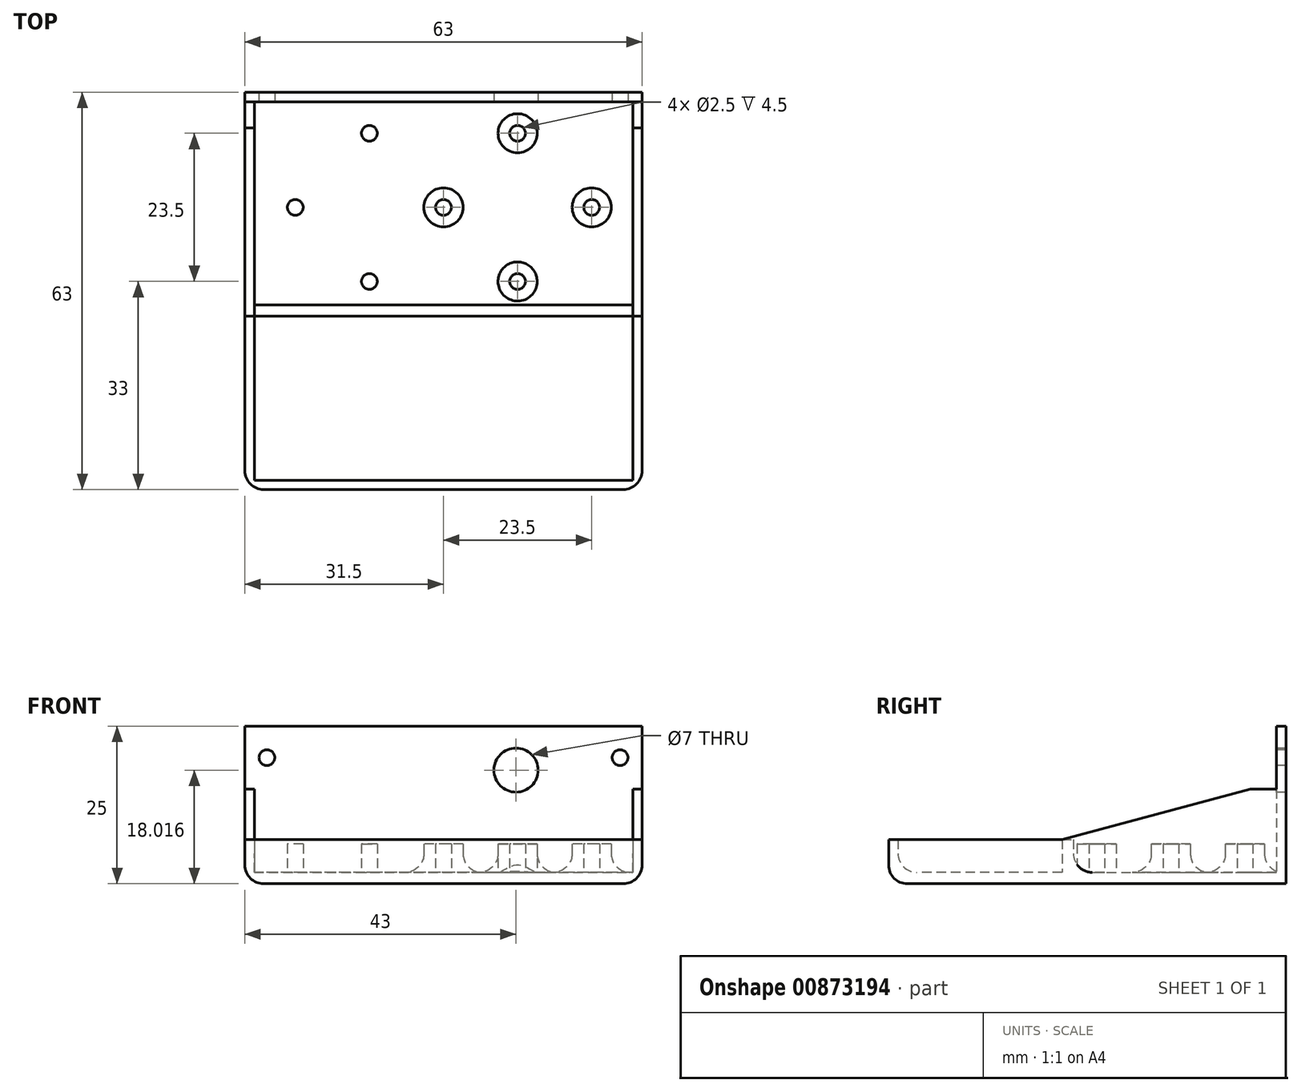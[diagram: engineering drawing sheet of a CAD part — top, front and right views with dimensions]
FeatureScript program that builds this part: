
annotation { "Feature Type Name" : "Feature", "Feature Type Description" : "" }
export const myFeature = defineFeature(function(context is Context, id is Id, definition is map)
    precondition{}
    {
        {
            var Q0;
            Q0=qCreatedBy(makeId("Top.planeOp"),FACE);
            var sketch = newSketch(context, id + "F0", { "sketchPlane" : qUnion([Q0])});
            skLineSegment(sketch, "E0.bottom", {"start": v(30, -30) * mm, "end": v(-30, -30) * mm});
            skLineSegment(sketch, "E0.top", {"start": v(30, 30) * mm, "end": v(-30, 30) * mm});
            skLineSegment(sketch, "E0.left", {"start": v(30, -30) * mm, "end": v(30, 30) * mm});
            skLineSegment(sketch, "E0.right", {"start": v(-30, -30) * mm, "end": v(-30, 30) * mm});
            skPoint(sketch, "E0.middle", {"position": v(0, 0) * mm});
            skLineSegment(sketch, "E1.bottom", {"start": v(31.5, -31.5) * mm, "end": v(-31.5, -31.5) * mm});
            skLineSegment(sketch, "E1.top", {"start": v(31.5, 31.5) * mm, "end": v(-31.5, 31.5) * mm});
            skLineSegment(sketch, "E1.left", {"start": v(31.5, -31.5) * mm, "end": v(31.5, 31.5) * mm});
            skLineSegment(sketch, "E1.right", {"start": v(-31.5, -31.5) * mm, "end": v(-31.5, 31.5) * mm});
            skLineSegment(sketch, "E2.bottom", {"start": v(52.1, -40) * mm, "end": v(-52.1, -40) * mm});
            skLineSegment(sketch, "E2.top", {"start": v(52.1, 40) * mm, "end": v(-52.1, 40) * mm});
            skLineSegment(sketch, "E2.left", {"start": v(52.1, -40) * mm, "end": v(52.1, 40) * mm});
            skLineSegment(sketch, "E2.right", {"start": v(-52.1, -40) * mm, "end": v(-52.1, 40) * mm});
            skLineSegment(sketch, "E3", {"start": v(-31.5, 31.5) * mm, "end": v(-31.5, 40) * mm});
            skLineSegment(sketch, "E4", {"start": v(-31.5, -31.5) * mm, "end": v(-31.5, -40) * mm});
            skLineSegment(sketch, "E5", {"start": v(-21.73, -30) * mm, "end": v(-21.73, -4) * mm, "construction": true});
            skLineSegment(sketch, "E6.bottom", {"start": v(-30, -4) * mm, "end": v(30, -4) * mm});
            skLineSegment(sketch, "E6.top", {"start": v(-30, -2.2) * mm, "end": v(30, -2.2) * mm});
            skLineSegment(sketch, "E6.left", {"start": v(-30, -4) * mm, "end": v(-30, -2.2) * mm});
            skLineSegment(sketch, "E6.right", {"start": v(30, -4) * mm, "end": v(30, -2.2) * mm});
            skLineSegment(sketch, "E7.bottom", {"start": v(-35.7, -5) * mm, "end": v(-31.5, -5) * mm});
            skLineSegment(sketch, "E7.top", {"start": v(-35.7, 5) * mm, "end": v(-31.5, 5) * mm});
            skLineSegment(sketch, "E7.left", {"start": v(-35.7, -5) * mm, "end": v(-35.7, 5) * mm});
            skPoint(sketch, "E7.middle", {"position": v(-31.5, 0) * mm});
            skPoint(sketch, "E7.right.start.orphan", {"position": v(-27.3, -5) * mm});
            skPoint(sketch, "E8.trimOffspring.end.orphan", {"position": v(-27.3, 5) * mm});
            skLineSegment(sketch, "E9.bottom", {"start": v(52.1, -40) * mm, "end": v(64.1, -40) * mm});
            skLineSegment(sketch, "E9.top", {"start": v(52.1, -28) * mm, "end": v(64.1, -28) * mm});
            skLineSegment(sketch, "E9.left", {"start": v(52.1, -40) * mm, "end": v(52.1, -28) * mm});
            skLineSegment(sketch, "E9.right", {"start": v(67.1, -37) * mm, "end": v(67.1, -31) * mm});
            skCircle(sketch, "E10", {"center": v(59.6, -34) * mm, "radius": 1.5 * mm});
            skPoint(sketch, "E10.centerSnap0", {"position": v(67.1, -34) * mm});
            skPoint(sketch, "E10.centerSnap1", {"position": v(59.6, -28) * mm});
            skPoint(sketch, "E11.visualSharp", {"position": v(67.1, -28) * mm});
            skArc(sketch, "E11.filletArc", {"start": v(67.1, -31) * mm, "mid": v(66.22, -28.88) * mm, "end": v(64.1, -28) * mm});
            skPoint(sketch, "E12.visualSharp", {"position": v(67.1, -40) * mm});
            skArc(sketch, "E12.filletArc", {"start": v(64.1, -40) * mm, "mid": v(66.22, -39.12) * mm, "end": v(67.1, -37) * mm});
            skLineSegment(sketch, "E13", {"start": v(0, 0) * mm, "end": v(11.58, 0) * mm, "construction": true});
            skLineSegment(sketch, "E14.MirrorCS", {"start": v(67.1, 37) * mm, "end": v(67.1, 31) * mm});
            skPoint(sketch, "E15.MirrorP", {"position": v(59.6, 28) * mm});
            skCircle(sketch, "E16.MirrorC", {"center": v(59.6, 34) * mm, "radius": 1.5 * mm});
            skLineSegment(sketch, "E17.MirrorCS", {"start": v(52.1, 28) * mm, "end": v(64.1, 28) * mm});
            skPoint(sketch, "E18.MirrorP", {"position": v(67.1, 28) * mm});
            skArc(sketch, "E19.MirrorCS", {"start": v(67.1, 31) * mm, "mid": v(66.22, 28.88) * mm, "end": v(64.1, 28) * mm});
            skPoint(sketch, "E20.MirrorP", {"position": v(67.1, 40) * mm});
            skLineSegment(sketch, "E21.MirrorCS", {"start": v(52.1, 40) * mm, "end": v(64.1, 40) * mm});
            skPoint(sketch, "E22.MirrorP", {"position": v(67.1, 34) * mm});
            skArc(sketch, "E23.MirrorCS", {"start": v(64.1, 40) * mm, "mid": v(66.22, 39.12) * mm, "end": v(67.1, 37) * mm});
            skLineSegment(sketch, "E24", {"start": v(0, 31.5) * mm, "end": v(0, 40) * mm});
            skLineSegment(sketch, "E25", {"start": v(-4, -31.5) * mm, "end": v(-4, -38.7) * mm});
            skLineSegment(sketch, "E26", {"start": v(-4, -38.7) * mm, "end": v(-31.5, -38.7) * mm});
            skLineSegment(sketch, "E27", {"start": v(-4, -38.7) * mm, "end": v(-4, -40) * mm});
            skLineSegment(sketch, "E28", {"start": v(-30, 30) * mm, "end": v(-31.5, 30) * mm});
            skLineSegment(sketch, "E29", {"start": v(30, 30) * mm, "end": v(31.5, 30) * mm});
            skLineSegment(sketch, "E30", {"start": v(-30, -4) * mm, "end": v(-31.5, -4) * mm});
            skLineSegment(sketch, "E31", {"start": v(30, -4) * mm, "end": v(31.5, -4) * mm});
            skSolve(sketch);
        }
        {
            var Q0;
            Q0=makeQuery(id+"F0.imprint","IMPRINT",FACE,{"disambiguationData":[TD([[makeQuery(id+"F0.imprint","IMPRINT",EDGE,{"derivedFrom":sQuery(id+"F0.wireOp",EDGE,"E0.top")}),-1.0]])]});
            extrude(context, id + "F1", {"entities" : qUnion([Q0]), "depth" : 25 * mm, "offsetDistance" : 25 * mm});
        }
        {
            var Q0;
            {var subQ0=sQuery(id+"F0.wireOp",EDGE,"E0.bottom");Q0=makeQuery(id+"F0.imprint","IMPRINT",FACE,{"disambiguationData":[TD([[makeQuery(id+"F0.imprint","IMPRINT",EDGE,{"derivedFrom":subQ0}),-1.0]])]});}
            var Q1;
            {var subQ1=sQuery(id+"F0.wireOp",EDGE,"E0.bottom");Q1=makeQuery(id+"F0.imprint","IMPRINT",FACE,{"disambiguationData":[TD([[makeQuery(id+"F0.imprint","IMPRINT",EDGE,{"derivedFrom":subQ1}),1.0]])]});}
            var Q2;
            {var subQ0=sQuery(id+"F0.wireOp",EDGE,"E0.top");Q2=makeQuery(id+"F0.imprint","IMPRINT",FACE,{"disambiguationData":[TD([[makeQuery(id+"F0.imprint","IMPRINT",EDGE,{"derivedFrom":subQ0}),1.0]])]});}
            var Q3;
            {var subQ2=sQuery(id+"F0.wireOp",EDGE,"E6.bottom");Q3=makeQuery(id+"F0.imprint","IMPRINT",FACE,{"disambiguationData":[TD([[makeQuery(id+"F0.imprint","IMPRINT",EDGE,{"derivedFrom":subQ2}),1.0]])]});}
            extrude(context, id + "F2", {"entities" : qUnion([Q0, Q1, Q2, Q3]), "operationType" : NewBodyOperationType.ADD, "depth" : 1.8 * mm, "offsetDistance" : 25 * mm});
        }
        {
            var Q0;
            {var subQ2=sQuery(id+"F0.wireOp",EDGE,"E6.bottom");Q0=makeQuery(id+"F0.imprint","IMPRINT",FACE,{"disambiguationData":[TD([[makeQuery(id+"F0.imprint","IMPRINT",EDGE,{"derivedFrom":subQ2}),1.0]])]});}
            extrude(context, id + "F3", {"entities" : qUnion([Q0]), "operationType" : NewBodyOperationType.ADD, "depth" : 7 * mm, "offsetDistance" : 25 * mm});
        }
        {
            var Q0;
            Q0=qCreatedBy(makeId("Top.planeOp"),FACE);
            var sketch = newSketch(context, id + "F4", { "sketchPlane" : qUnion([Q0])});
            skLineSegment(sketch, "E32", {"start": v(0, 0) * mm, "end": v(0, 0) * mm});
            skLineSegment(sketch, "E33", {"start": v(0, 0) * mm, "end": v(0, 1.5) * mm, "construction": true});
            skCircle(sketch, "E34", {"center": v(0, 1.5) * mm, "radius": 1.25 * mm});
            skCircle(sketch, "E35", {"center": v(0, 1.5) * mm, "radius": 3.1 * mm});
            skCircle(sketch, "E36.0.1.0", {"center": v(0, 13.25) * mm, "radius": 3.1 * mm});
            skCircle(sketch, "E36.0.1.1", {"center": v(0, 13.25) * mm, "radius": 1.25 * mm});
            skCircle(sketch, "E36.0.2.0", {"center": v(0, 25) * mm, "radius": 3.1 * mm});
            skCircle(sketch, "E36.0.2.1", {"center": v(0, 25) * mm, "radius": 1.25 * mm});
            skCircle(sketch, "E36.1.0.0", {"center": v(11.75, 1.5) * mm, "radius": 3.1 * mm});
            skCircle(sketch, "E36.1.0.1", {"center": v(11.75, 1.5) * mm, "radius": 1.25 * mm});
            skCircle(sketch, "E36.1.1.0", {"center": v(11.75, 13.25) * mm, "radius": 3.1 * mm});
            skCircle(sketch, "E36.1.1.1", {"center": v(11.75, 13.25) * mm, "radius": 1.25 * mm});
            skCircle(sketch, "E36.1.2.0", {"center": v(11.75, 25) * mm, "radius": 3.1 * mm});
            skCircle(sketch, "E36.1.2.1", {"center": v(11.75, 25) * mm, "radius": 1.25 * mm});
            skCircle(sketch, "E36.2.0.0", {"center": v(23.5, 1.5) * mm, "radius": 3.1 * mm});
            skCircle(sketch, "E36.2.0.1", {"center": v(23.5, 1.5) * mm, "radius": 1.25 * mm});
            skCircle(sketch, "E36.2.1.0", {"center": v(23.5, 13.25) * mm, "radius": 3.1 * mm});
            skCircle(sketch, "E36.2.1.1", {"center": v(23.5, 13.25) * mm, "radius": 1.25 * mm});
            skCircle(sketch, "E36.2.2.0", {"center": v(23.5, 25) * mm, "radius": 3.1 * mm});
            skCircle(sketch, "E36.2.2.1", {"center": v(23.5, 25) * mm, "radius": 1.25 * mm});
            skCircle(sketch, "E36.3.0.0", {"center": v(35.25, 1.5) * mm, "radius": 3.1 * mm});
            skCircle(sketch, "E36.3.0.1", {"center": v(35.25, 1.5) * mm, "radius": 1.25 * mm});
            skCircle(sketch, "E36.3.1.0", {"center": v(35.25, 13.25) * mm, "radius": 3.1 * mm});
            skCircle(sketch, "E36.3.1.1", {"center": v(35.25, 13.25) * mm, "radius": 1.25 * mm});
            skCircle(sketch, "E36.3.2.0", {"center": v(35.25, 25) * mm, "radius": 3.1 * mm});
            skCircle(sketch, "E36.3.2.1", {"center": v(35.25, 25) * mm, "radius": 1.25 * mm});
            skCircle(sketch, "E36.4.0.0", {"center": v(47, 1.5) * mm, "radius": 3.1 * mm});
            skCircle(sketch, "E36.4.0.1", {"center": v(47, 1.5) * mm, "radius": 1.25 * mm});
            skCircle(sketch, "E36.4.1.0", {"center": v(47, 13.25) * mm, "radius": 3.1 * mm});
            skCircle(sketch, "E36.4.1.1", {"center": v(47, 13.25) * mm, "radius": 1.25 * mm});
            skCircle(sketch, "E36.4.2.0", {"center": v(47, 25) * mm, "radius": 3.1 * mm});
            skCircle(sketch, "E36.4.2.1", {"center": v(47, 25) * mm, "radius": 1.25 * mm});
            skLineSegment(sketch, "E36.direction1", {"start": v(0, 1.5) * mm, "end": v(11.75, 1.5) * mm, "construction": true});
            skLineSegment(sketch, "E36.direction2", {"start": v(0, 1.5) * mm, "end": v(0, 13.25) * mm, "construction": true});
            skCircle(sketch, "E37.MirrorC", {"center": v(-11.75, 1.5) * mm, "radius": 1.25 * mm});
            skCircle(sketch, "E38.MirrorC", {"center": v(-35.25, 25) * mm, "radius": 1.25 * mm});
            skCircle(sketch, "E39.MirrorC", {"center": v(-47, 25) * mm, "radius": 1.25 * mm});
            skCircle(sketch, "E40.MirrorC", {"center": v(-11.75, 25) * mm, "radius": 1.25 * mm});
            skCircle(sketch, "E41.MirrorC", {"center": v(-47, 1.5) * mm, "radius": 1.25 * mm});
            skCircle(sketch, "E42.MirrorC", {"center": v(-47, 13.25) * mm, "radius": 1.25 * mm});
            skCircle(sketch, "E43.MirrorC", {"center": v(-11.75, 13.25) * mm, "radius": 1.25 * mm});
            skCircle(sketch, "E44.MirrorC", {"center": v(-23.5, 25) * mm, "radius": 1.25 * mm});
            skCircle(sketch, "E45.MirrorC", {"center": v(-23.5, 1.5) * mm, "radius": 1.25 * mm});
            skCircle(sketch, "E46.MirrorC", {"center": v(-35.25, 1.5) * mm, "radius": 1.25 * mm});
            skCircle(sketch, "E47.MirrorC", {"center": v(-35.25, 13.25) * mm, "radius": 1.25 * mm});
            skCircle(sketch, "E48.MirrorC", {"center": v(-23.5, 13.25) * mm, "radius": 1.25 * mm});
            skCircle(sketch, "E49.MirrorC", {"center": v(-11.75, 13.25) * mm, "radius": 3.1 * mm});
            skCircle(sketch, "E50.MirrorC", {"center": v(-35.25, 25) * mm, "radius": 3.1 * mm});
            skCircle(sketch, "E51.MirrorC", {"center": v(-47, 25) * mm, "radius": 3.1 * mm});
            skCircle(sketch, "E52.MirrorC", {"center": v(-35.25, 1.5) * mm, "radius": 3.1 * mm});
            skCircle(sketch, "E53.MirrorC", {"center": v(-47, 13.25) * mm, "radius": 3.1 * mm});
            skCircle(sketch, "E54.MirrorC", {"center": v(-23.5, 25) * mm, "radius": 3.1 * mm});
            skCircle(sketch, "E55.MirrorC", {"center": v(-11.75, 1.5) * mm, "radius": 3.1 * mm});
            skCircle(sketch, "E56.MirrorC", {"center": v(-35.25, 13.25) * mm, "radius": 3.1 * mm});
            skCircle(sketch, "E57.MirrorC", {"center": v(-47, 1.5) * mm, "radius": 3.1 * mm});
            skCircle(sketch, "E58.MirrorC", {"center": v(-11.75, 25) * mm, "radius": 3.1 * mm});
            skCircle(sketch, "E59.MirrorC", {"center": v(-23.5, 1.5) * mm, "radius": 3.1 * mm});
            skCircle(sketch, "E60.MirrorC", {"center": v(-23.5, 13.25) * mm, "radius": 3.1 * mm});
            skCircle(sketch, "E61.MirrorC", {"center": v(-47, -10.25) * mm, "radius": 3.1 * mm});
            skCircle(sketch, "E62.MirrorC", {"center": v(-47, -10.25) * mm, "radius": 1.25 * mm});
            skSolve(sketch);
        }
        {
            var Q0;
            Q0=makeQuery(id+"F4.imprint","IMPRINT",FACE,{"disambiguationData":[TD([[makeQuery(id+"F4.imprint","IMPRINT",EDGE,{"derivedFrom":sQuery(id+"F4.wireOp",EDGE,"E36.2.1.0")}),1.0]])]});
            var Q1;
            Q1=makeQuery(id+"F4.imprint","IMPRINT",FACE,{"disambiguationData":[TD([[makeQuery(id+"F4.imprint","IMPRINT",EDGE,{"derivedFrom":sQuery(id+"F4.wireOp",EDGE,"E36.1.0.0")}),1.0]])]});
            var Q2;
            Q2=makeQuery(id+"F4.imprint","IMPRINT",FACE,{"disambiguationData":[TD([[makeQuery(id+"F4.imprint","IMPRINT",EDGE,{"derivedFrom":sQuery(id+"F4.wireOp",EDGE,"E36.1.2.0")}),1.0]])]});
            var Q3;
            Q3=makeQuery(id+"F4.imprint","IMPRINT",FACE,{"disambiguationData":[TD([[makeQuery(id+"F4.imprint","IMPRINT",EDGE,{"derivedFrom":sQuery(id+"F4.wireOp",EDGE,"E36.0.1.0")}),1.0]])]});
            var Q4;
            Q4=makeQuery(id+"F4.imprint","IMPRINT",FACE,{"disambiguationData":[TD([[makeQuery(id+"F4.imprint","IMPRINT",EDGE,{"derivedFrom":sQuery(id+"F4.wireOp",EDGE,"E40.MirrorC")}),1.0]])]});
            var Q5;
            Q5=makeQuery(id+"F4.imprint","IMPRINT",FACE,{"disambiguationData":[TD([[makeQuery(id+"F4.imprint","IMPRINT",EDGE,{"derivedFrom":sQuery(id+"F4.wireOp",EDGE,"E37.MirrorC")}),1.0]])]});
            var Q6;
            Q6=makeQuery(id+"F4.imprint","IMPRINT",FACE,{"disambiguationData":[TD([[makeQuery(id+"F4.imprint","IMPRINT",EDGE,{"derivedFrom":sQuery(id+"F4.wireOp",EDGE,"E48.MirrorC")}),1.0]])]});
            extrude(context, id + "F5", {"entities" : qUnion([Q0, Q1, Q2, Q3, Q4, Q5, Q6]), "operationType" : NewBodyOperationType.ADD, "depth" : (4.5 + 1.8) * mm, "offsetDistance" : 25 * mm});
        }
        {
            var Q0;
            {var subQ2=sQuery(id+"F0.wireOp",EDGE,"E28");Q0=makeQuery(id+"F0.imprint","IMPRINT",FACE,{"disambiguationData":[TD([[makeQuery(id+"F0.imprint","IMPRINT",EDGE,{"derivedFrom":subQ2}),1.0]])]});}
            var Q1;
            {var subQ0=sQuery(id+"F0.wireOp",EDGE,"E29");Q1=makeQuery(id+"F0.imprint","IMPRINT",FACE,{"disambiguationData":[TD([[makeQuery(id+"F0.imprint","IMPRINT",EDGE,{"derivedFrom":subQ0}),-1.0]])]});}
            extrude(context, id + "F6", {"entities" : qUnion([Q0, Q1]), "operationType" : NewBodyOperationType.ADD, "depth" : 15 * mm, "offsetDistance" : 25 * mm});
        }
        {
            var Q0;
            {var subQ1=sQuery(id+"F0.wireOp",EDGE,"E0.bottom");Q0=makeQuery(id+"F0.imprint","IMPRINT",FACE,{"disambiguationData":[TD([[makeQuery(id+"F0.imprint","IMPRINT",EDGE,{"derivedFrom":subQ1}),1.0]])]});}
            extrude(context, id + "F7", {"entities" : qUnion([Q0]), "operationType" : NewBodyOperationType.ADD, "depth" : 7 * mm, "offsetDistance" : 25 * mm});
        }
        {
            var Q0;
            Q0=makeQuery(id+"F6.opExtrude","CAP_EDGE",EDGE,{"disambiguationData":[OSD([sQuery(id+"F0.wireOp",EDGE,"E30")])],"isStart":false});
            chamfer(context, id + "F8", {"entities" : qUnion([Q0]), "chamferType" : ChamferType.OFFSET_ANGLE, "width" : 8 * mm, "oppositeDirection" : false, "angle" : 75 * degree, "tangentPropagation" : true});
        }
        {
            var Q0;
            Q0=makeQuery(id+"F6.opExtrude","CAP_EDGE",EDGE,{"disambiguationData":[OSD([sQuery(id+"F0.wireOp",EDGE,"E31")])],"isStart":false});
            chamfer(context, id + "F9", {"entities" : qUnion([Q0]), "chamferType" : ChamferType.OFFSET_ANGLE, "width" : 8 * mm, "oppositeDirection" : true, "angle" : 75 * degree, "tangentPropagation" : true});
        }
        {
            var Q0;
            Q0=qCreatedBy(makeId("Front.planeOp"),FACE);
            var sketch = newSketch(context, id + "F10", { "sketchPlane" : qUnion([Q0])});
            skLineSegment(sketch, "E63", {"start": v(0, 0) * mm, "end": v(0, 20) * mm, "construction": true});
            skLineSegment(sketch, "E64", {"start": v(0, 20) * mm, "end": v(28, 20) * mm, "construction": true});
            skCircle(sketch, "E65", {"center": v(28, 20) * mm, "radius": 1.25 * mm});
            skCircle(sketch, "E66.MirrorC", {"center": v(-28, 20) * mm, "radius": 1.25 * mm});
            skLineSegment(sketch, "E67", {"start": v(0, 18.02) * mm, "end": v(11.5, 18.02) * mm, "construction": true});
            skCircle(sketch, "E68", {"center": v(11.5, 18.02) * mm, "radius": 3.5 * mm});
            skSolve(sketch);
        }
        {
            var Q0;
            Q0 = qSketchRegion(id + "F10", true);
            extrude(context, id + "F11", {"entities" : qUnion([Q0]), "operationType" : NewBodyOperationType.REMOVE, "endBound" : BoundingType.THROUGH_ALL, "oppositeDirection" : true, "depth" : 25 * mm, "offsetDistance" : 25 * mm});
        }
        {
            var Q0;
            Q0=makeQuery(id+"F2.opExtrude","CAP_EDGE",EDGE,{"disambiguationData":[OSD([sQuery(id+"F0.wireOp",EDGE,"E0.top")])],"isStart":false});
            var Q1;
            {var subQ0=sQuery(id+"F0.wireOp",EDGE,"E0.left");var subQ1=sQuery(id+"F0.wireOp",EDGE,"E0.right");var subQ2=sQuery(id+"F0.wireOp",EDGE,"E0.top");Q1=makeQuery(id+"F5.boolean.opBoolean","INTERSECT",EDGE,{"derivedFrom":[makeQuery(id+"F3.boolean.opBoolean","SPLIT",FACE,{"disambiguationData":[TD([makeQuery(id+"F3.opExtrude","SWEPT_FACE",FACE,{"disambiguationData":[OSD([sQuery(id+"F0.wireOp",EDGE,"E6.top")])]})])],"derivedFrom":makeQuery(id+"F2.opExtrude","CAP_FACE",FACE,{"disambiguationData":[OSD([subQ2,subQ0,subQ1,sQuery(id+"F0.wireOp",EDGE,"E1.bottom"),sQuery(id+"F0.wireOp",EDGE,"E1.left"),sQuery(id+"F0.wireOp",EDGE,"E1.right"),sQuery(id+"F0.wireOp",EDGE,"E30"),sQuery(id+"F0.wireOp",EDGE,"E31")])],"isStart":false})}),makeQuery(id+"F5.opExtrude","SWEPT_FACE",FACE,{"disambiguationData":[OSD([sQuery(id+"F4.wireOp",EDGE,"E58.MirrorC")])]})]});}
            var Q2;
            {var subQ0=sQuery(id+"F0.wireOp",EDGE,"E0.left");var subQ1=sQuery(id+"F0.wireOp",EDGE,"E0.right");var subQ2=sQuery(id+"F0.wireOp",EDGE,"E0.top");Q2=makeQuery(id+"F5.boolean.opBoolean","INTERSECT",EDGE,{"derivedFrom":[makeQuery(id+"F3.boolean.opBoolean","SPLIT",FACE,{"disambiguationData":[TD([makeQuery(id+"F3.opExtrude","SWEPT_FACE",FACE,{"disambiguationData":[OSD([sQuery(id+"F0.wireOp",EDGE,"E6.top")])]})])],"derivedFrom":makeQuery(id+"F2.opExtrude","CAP_FACE",FACE,{"disambiguationData":[OSD([subQ2,subQ0,subQ1,sQuery(id+"F0.wireOp",EDGE,"E1.bottom"),sQuery(id+"F0.wireOp",EDGE,"E1.left"),sQuery(id+"F0.wireOp",EDGE,"E1.right"),sQuery(id+"F0.wireOp",EDGE,"E30"),sQuery(id+"F0.wireOp",EDGE,"E31")])],"isStart":false})}),makeQuery(id+"F5.opExtrude","SWEPT_FACE",FACE,{"disambiguationData":[OSD([sQuery(id+"F4.wireOp",EDGE,"E60.MirrorC")])]})]});}
            var Q3;
            {var subQ0=sQuery(id+"F0.wireOp",EDGE,"E0.left");var subQ1=sQuery(id+"F0.wireOp",EDGE,"E0.right");var subQ2=sQuery(id+"F0.wireOp",EDGE,"E0.top");Q3=makeQuery(id+"F5.boolean.opBoolean","INTERSECT",EDGE,{"derivedFrom":[makeQuery(id+"F3.boolean.opBoolean","SPLIT",FACE,{"disambiguationData":[TD([makeQuery(id+"F3.opExtrude","SWEPT_FACE",FACE,{"disambiguationData":[OSD([sQuery(id+"F0.wireOp",EDGE,"E6.top")])]})])],"derivedFrom":makeQuery(id+"F2.opExtrude","CAP_FACE",FACE,{"disambiguationData":[OSD([subQ2,subQ0,subQ1,sQuery(id+"F0.wireOp",EDGE,"E1.bottom"),sQuery(id+"F0.wireOp",EDGE,"E1.left"),sQuery(id+"F0.wireOp",EDGE,"E1.right"),sQuery(id+"F0.wireOp",EDGE,"E30"),sQuery(id+"F0.wireOp",EDGE,"E31")])],"isStart":false})}),makeQuery(id+"F5.opExtrude","SWEPT_FACE",FACE,{"disambiguationData":[OSD([sQuery(id+"F4.wireOp",EDGE,"E36.0.1.0")])]})]});}
            var Q4;
            {var subQ0=sQuery(id+"F0.wireOp",EDGE,"E0.left");var subQ1=sQuery(id+"F0.wireOp",EDGE,"E0.right");var subQ2=sQuery(id+"F0.wireOp",EDGE,"E0.top");Q4=makeQuery(id+"F5.boolean.opBoolean","INTERSECT",EDGE,{"derivedFrom":[makeQuery(id+"F3.boolean.opBoolean","SPLIT",FACE,{"disambiguationData":[TD([makeQuery(id+"F3.opExtrude","SWEPT_FACE",FACE,{"disambiguationData":[OSD([sQuery(id+"F0.wireOp",EDGE,"E6.top")])]})])],"derivedFrom":makeQuery(id+"F2.opExtrude","CAP_FACE",FACE,{"disambiguationData":[OSD([subQ2,subQ0,subQ1,sQuery(id+"F0.wireOp",EDGE,"E1.bottom"),sQuery(id+"F0.wireOp",EDGE,"E1.left"),sQuery(id+"F0.wireOp",EDGE,"E1.right"),sQuery(id+"F0.wireOp",EDGE,"E30"),sQuery(id+"F0.wireOp",EDGE,"E31")])],"isStart":false})}),makeQuery(id+"F5.opExtrude","SWEPT_FACE",FACE,{"disambiguationData":[OSD([sQuery(id+"F4.wireOp",EDGE,"E36.1.2.0")])]})]});}
            var Q5;
            {var subQ0=sQuery(id+"F0.wireOp",EDGE,"E0.left");var subQ1=sQuery(id+"F0.wireOp",EDGE,"E0.right");var subQ2=sQuery(id+"F0.wireOp",EDGE,"E0.top");Q5=makeQuery(id+"F5.boolean.opBoolean","INTERSECT",EDGE,{"derivedFrom":[makeQuery(id+"F3.boolean.opBoolean","SPLIT",FACE,{"disambiguationData":[TD([makeQuery(id+"F3.opExtrude","SWEPT_FACE",FACE,{"disambiguationData":[OSD([sQuery(id+"F0.wireOp",EDGE,"E6.top")])]})])],"derivedFrom":makeQuery(id+"F2.opExtrude","CAP_FACE",FACE,{"disambiguationData":[OSD([subQ2,subQ0,subQ1,sQuery(id+"F0.wireOp",EDGE,"E1.bottom"),sQuery(id+"F0.wireOp",EDGE,"E1.left"),sQuery(id+"F0.wireOp",EDGE,"E1.right"),sQuery(id+"F0.wireOp",EDGE,"E30"),sQuery(id+"F0.wireOp",EDGE,"E31")])],"isStart":false})}),makeQuery(id+"F5.opExtrude","SWEPT_FACE",FACE,{"disambiguationData":[OSD([sQuery(id+"F4.wireOp",EDGE,"E36.2.1.0")])]})]});}
            var Q6;
            Q6=makeQuery(id+"F3.boolean.opBoolean","INTERSECT",EDGE,{"derivedFrom":[makeQuery(id+"F2.opExtrude","CAP_FACE",FACE,{"disambiguationData":[OSD([sQuery(id+"F0.wireOp",EDGE,"E0.top"),sQuery(id+"F0.wireOp",EDGE,"E0.left"),sQuery(id+"F0.wireOp",EDGE,"E0.right"),sQuery(id+"F0.wireOp",EDGE,"E1.bottom"),sQuery(id+"F0.wireOp",EDGE,"E1.left"),sQuery(id+"F0.wireOp",EDGE,"E1.right"),sQuery(id+"F0.wireOp",EDGE,"E30"),sQuery(id+"F0.wireOp",EDGE,"E31")])],"isStart":false}),makeQuery(id+"F3.opExtrude","SWEPT_FACE",FACE,{"disambiguationData":[OSD([sQuery(id+"F0.wireOp",EDGE,"E6.top")])]})]});
            var Q7;
            {var subQ0=sQuery(id+"F0.wireOp",EDGE,"E4");var subQ1=sQuery(id+"F0.wireOp",EDGE,"E1.right");var subQ2=sQuery(id+"F0.wireOp",EDGE,"E1.bottom");Q7=makeQuery(id+"F7.boolean.opBoolean","MERGE",EDGE,{"derivedFrom":[makeQuery(id+"F2.opExtrude","SWEPT_EDGE",EDGE,{"disambiguationData":[OSD([subQ2,subQ1,subQ0])]}),makeQuery(id+"F7.opExtrude","SWEPT_EDGE",EDGE,{"disambiguationData":[OSD([subQ2,subQ1,subQ0])]})]});}
            var Q8;
            {var subQ0=sQuery(id+"F0.wireOp",EDGE,"E1.left");var subQ1=sQuery(id+"F0.wireOp",EDGE,"E1.bottom");Q8=makeQuery(id+"F7.boolean.opBoolean","MERGE",EDGE,{"derivedFrom":[makeQuery(id+"F2.opExtrude","SWEPT_EDGE",EDGE,{"disambiguationData":[OSD([subQ1,subQ0])]}),makeQuery(id+"F7.opExtrude","SWEPT_EDGE",EDGE,{"disambiguationData":[OSD([subQ1,subQ0])]})]});}
            var Q9;
            Q9=makeQuery(id+"F2.opExtrude","CAP_EDGE",EDGE,{"disambiguationData":[OSD([sQuery(id+"F0.wireOp",EDGE,"E1.bottom")])],"isStart":true});
            var Q10;
            {var subQ0=sQuery(id+"F0.wireOp",EDGE,"E1.left");var subQ1=sQuery(id+"F0.wireOp",EDGE,"E1.bottom");var subQ2=sQuery(id+"F0.wireOp",EDGE,"E0.right");var subQ3=sQuery(id+"F0.wireOp",EDGE,"E0.left");var subQ4=sQuery(id+"F0.wireOp",EDGE,"E1.right");var subQ5=sQuery(id+"F0.wireOp",EDGE,"E30");var subQ6=sQuery(id+"F0.wireOp",EDGE,"E31");Q10=makeQuery(id+"F7.boolean.opBoolean","INTERSECT",EDGE,{"derivedFrom":[makeQuery(id+"F3.boolean.opBoolean","SPLIT",FACE,{"disambiguationData":[TD([makeQuery(id+"F2.opExtrude","SWEPT_FACE",FACE,{"disambiguationData":[OSD([subQ1])]})])],"derivedFrom":makeQuery(id+"F2.opExtrude","CAP_FACE",FACE,{"disambiguationData":[OSD([sQuery(id+"F0.wireOp",EDGE,"E0.top"),subQ3,subQ2,subQ1,subQ0,subQ4,subQ5,subQ6])],"isStart":false})}),makeQuery(id+"F7.opExtrude","SWEPT_FACE",FACE,{"disambiguationData":[OSD([sQuery(id+"F0.wireOp",EDGE,"E0.bottom")])]})]});}
            var Q11;
            Q11=makeQuery(id+"F2.opExtrude","CAP_EDGE",EDGE,{"disambiguationData":[OSD([sQuery(id+"F0.wireOp",EDGE,"E0.right")])],"isStart":false});
            var Q12;
            Q12=makeQuery(id+"F2.opExtrude","CAP_EDGE",EDGE,{"disambiguationData":[OSD([sQuery(id+"F0.wireOp",EDGE,"E0.left")])],"isStart":false});
            var Q13;
            Q13=makeQuery(id+"F6.opExtrude","SWEPT_EDGE",EDGE,{"disambiguationData":[OSD([sQuery(id+"F0.wireOp",EDGE,"E0.top"),sQuery(id+"F0.wireOp",EDGE,"E0.left"),sQuery(id+"F0.wireOp",EDGE,"E29")])]});
            var Q14;
            Q14=makeQuery(id+"F6.opExtrude","SWEPT_EDGE",EDGE,{"disambiguationData":[OSD([sQuery(id+"F0.wireOp",EDGE,"E0.top"),sQuery(id+"F0.wireOp",EDGE,"E0.right"),sQuery(id+"F0.wireOp",EDGE,"E28")])]});
            var Q15;
            {var subQ0=sQuery(id+"F0.wireOp",EDGE,"E1.left");Q15=makeQuery(id+"F6.boolean.opBoolean","MERGE",EDGE,{"derivedFrom":[makeQuery(id+"F1.opExtrude","CAP_EDGE",EDGE,{"disambiguationData":[OSD([subQ0])],"isStart":true}),makeQuery(id+"F2.opExtrude","CAP_EDGE",EDGE,{"disambiguationData":[OSD([subQ0])],"isStart":true}),makeQuery(id+"F6.opExtrude","CAP_EDGE",EDGE,{"disambiguationData":[OSD([subQ0])],"isStart":true})]});}
            var Q16;
            {var subQ0=sQuery(id+"F0.wireOp",EDGE,"E1.right");Q16=makeQuery(id+"F6.boolean.opBoolean","MERGE",EDGE,{"derivedFrom":[makeQuery(id+"F1.opExtrude","CAP_EDGE",EDGE,{"disambiguationData":[OSD([subQ0])],"isStart":true}),makeQuery(id+"F2.opExtrude","CAP_EDGE",EDGE,{"disambiguationData":[OSD([subQ0])],"isStart":true}),makeQuery(id+"F6.opExtrude","CAP_EDGE",EDGE,{"disambiguationData":[OSD([subQ0])],"isStart":true})]});}
            fillet(context, id + "F12", {"entities" : qUnion([Q0, Q1, Q2, Q3, Q4, Q5, Q6, Q7, Q8, Q9, Q10, Q11, Q12, Q13, Q14, Q15, Q16]), "radius" : 3 * mm, "tangentPropagation" : true, "allowEdgeOverflow" : false});
        }
    });
